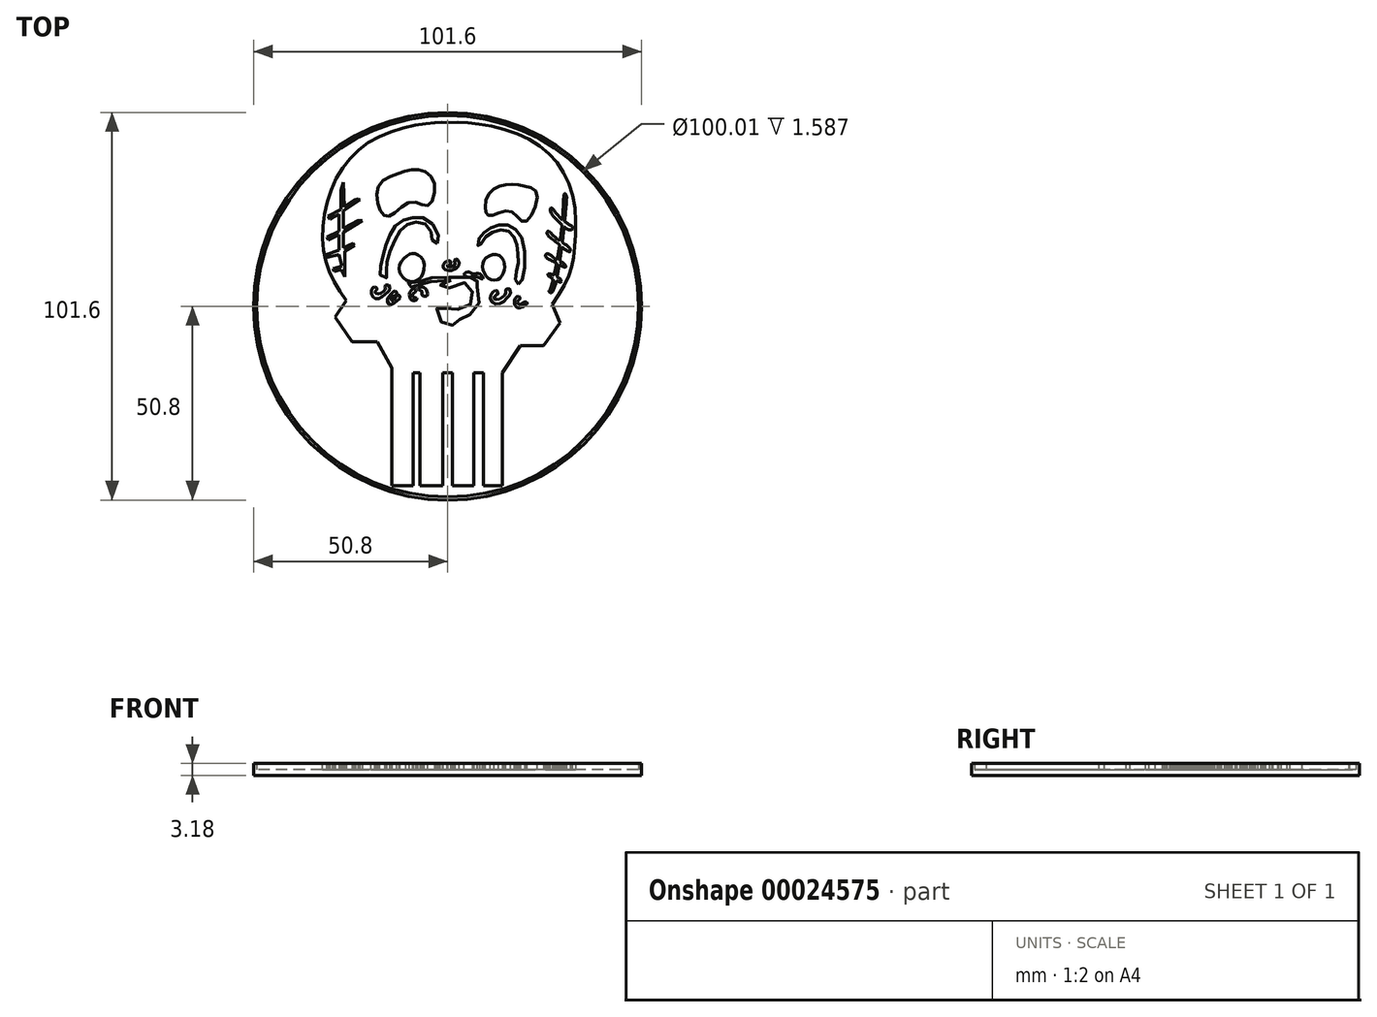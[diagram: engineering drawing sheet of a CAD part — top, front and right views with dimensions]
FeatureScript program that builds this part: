
annotation { "Feature Type Name" : "Feature", "Feature Type Description" : "" }
export const myFeature = defineFeature(function(context is Context, id is Id, definition is map)
    precondition{}
    {
        {
            var Q0;
            Q0=qCreatedBy(makeId("Top.planeOp"),FACE);
            var sketch = newSketch(context, id + "F0", { "sketchPlane" : qUnion([Q0])});
            skCircle(sketch, "E0", {"center": v(0, 0) * mm, "radius": 50.8 * mm});
            skSolve(sketch);
        }
        {
            var Q0;
            Q0 = qSketchRegion(id + "F0", true);
            extrude(context, id + "F1", {"entities" : qUnion([Q0]), "depth" : 1.59 * mm});
        }
        {
            var Q0;
            Q0=qCreatedBy(makeId("Top.planeOp"),FACE);
            var sketch = newSketch(context, id + "F2", { "sketchPlane" : qUnion([Q0])});
            skFitSpline(sketch, "E1", {"points": [v(-26.6, 1.46) * mm, v(-31.85, 11.54) * mm, v(-32.25, 24.2) * mm, v(-26.85, 37.18) * mm, v(-16.29, 45.16) * mm, v(-4.11, 48.07) * mm, v(0, 48.15) * mm], "startDerivative": vector(-36.73, 56.75) * mm, "endDerivative": vector(34.48, -1.2) * mm});
            skLineSegment(sketch, "E2", {"start": v(-26.6, 1.46) * mm, "end": v(-29.5, -2.79) * mm});
            skLineSegment(sketch, "E3", {"start": v(-29.5, -2.79) * mm, "end": v(-24.98, -9.3) * mm});
            skLineSegment(sketch, "E4", {"start": v(-24.98, -9.3) * mm, "end": v(-18.46, -9.3) * mm});
            skLineSegment(sketch, "E5", {"start": v(-18.46, -9.3) * mm, "end": v(-14.63, -16.12) * mm});
            skLineSegment(sketch, "E6", {"start": v(-14.63, -16.12) * mm, "end": v(-14.63, -47) * mm});
            skLineSegment(sketch, "E7", {"start": v(-14.63, -47) * mm, "end": v(-9.07, -47) * mm});
            skLineSegment(sketch, "E8", {"start": v(-9.07, -47) * mm, "end": v(-9.07, -17.46) * mm});
            skLineSegment(sketch, "E9", {"start": v(-9.07, -17.46) * mm, "end": v(-7.24, -17.46) * mm});
            skLineSegment(sketch, "E10", {"start": v(-7.24, -17.46) * mm, "end": v(-7.24, -47) * mm});
            skLineSegment(sketch, "E11", {"start": v(-7.24, -47) * mm, "end": v(-1.3, -47) * mm});
            skLineSegment(sketch, "E12", {"start": v(-1.3, -47) * mm, "end": v(-1.3, -17.46) * mm});
            skPoint(sketch, "E12.endSnap0", {"position": v(-8.15, -17.46) * mm});
            skLineSegment(sketch, "E13", {"start": v(-1.3, -17.46) * mm, "end": v(1.22, -17.46) * mm});
            skLineSegment(sketch, "E14", {"start": v(1.22, -17.46) * mm, "end": v(1.22, -47) * mm});
            skLineSegment(sketch, "E15", {"start": v(1.22, -47) * mm, "end": v(6.9, -47) * mm});
            skLineSegment(sketch, "E16", {"start": v(6.9, -47) * mm, "end": v(6.9, -17.46) * mm});
            skLineSegment(sketch, "E17", {"start": v(6.9, -17.46) * mm, "end": v(9.37, -17.46) * mm});
            skLineSegment(sketch, "E18", {"start": v(9.37, -17.46) * mm, "end": v(9.37, -47) * mm});
            skLineSegment(sketch, "E19", {"start": v(9.37, -47) * mm, "end": v(14.37, -47) * mm});
            skLineSegment(sketch, "E20", {"start": v(14.37, -47) * mm, "end": v(14.37, -17.46) * mm});
            skLineSegment(sketch, "E21", {"start": v(14.37, -17.46) * mm, "end": v(19.04, -10.32) * mm});
            skLineSegment(sketch, "E22", {"start": v(19.04, -10.32) * mm, "end": v(25.13, -10.32) * mm});
            skLineSegment(sketch, "E23", {"start": v(25.13, -10.32) * mm, "end": v(29.4, -4.4) * mm});
            skLineSegment(sketch, "E24", {"start": v(29.4, -4.4) * mm, "end": v(27.39, 0.48) * mm});
            skFitSpline(sketch, "E25", {"points": [v(27.39, 0.48) * mm, v(31.86, 8.27) * mm, v(33.2, 15.08) * mm, v(33.15, 27.34) * mm, v(28.8, 37.41) * mm, v(20.37, 44.27) * mm, v(8.12, 47.78) * mm, v(0, 48.15) * mm], "startDerivative": vector(38.96, 59.1) * mm, "endDerivative": vector(-60.1, -2.73) * mm});
            skFitSpline(sketch, "E26", {"points": [v(-18.15, 31.4) * mm, v(-12.69, 34.85) * mm, v(-7.7, 35.8) * mm, v(-3.58, 32.55) * mm, v(-5.11, 26.41) * mm, v(-9.43, 27.37) * mm, v(-14.99, 23.73) * mm, v(-17.39, 24.69) * mm, v(-18.15, 31.4) * mm]});
            skFitSpline(sketch, "E27", {"points": [v(10.8, 29.48) * mm, v(15.31, 31.88) * mm, v(20.2, 31.5) * mm, v(23.46, 29.2) * mm, v(20.1, 22.1) * mm, v(16.56, 24.88) * mm, v(11.38, 23.73) * mm, v(10.04, 24.59) * mm, v(10.8, 29.48) * mm]});
            skFitSpline(sketch, "E28", {"points": [v(-2.71, 16.53) * mm, v(-2.52, 18.93) * mm, v(-5.88, 23.06) * mm, v(-9.52, 23.15) * mm, v(-12.69, 22) * mm, v(-14.99, 18.93) * mm, v(-16.43, 15.2) * mm, v(-17.48, 10.97) * mm, v(-17.58, 8.1) * mm, v(-16.04, 7.42) * mm, v(-15.95, 9.25) * mm, v(-15.85, 12.12) * mm, v(-14.22, 16.44) * mm, v(-12.02, 20.37) * mm, v(-9.43, 21.8) * mm, v(-6.45, 21.9) * mm, v(-4.25, 19.32) * mm, v(-3.96, 17.1) * mm, v(-2.71, 16.53) * mm]});
            skFitSpline(sketch, "E29", {"points": [v(18.57, 5.8) * mm, v(19.72, 7.33) * mm, v(19.53, 17.5) * mm, v(16.37, 21.04) * mm, v(12.72, 21.14) * mm, v(9.75, 19.5) * mm, v(8.03, 17.3) * mm, v(8.12, 15.67) * mm, v(9.59, 17.62) * mm, v(12.16, 19.52) * mm, v(15.35, 19.86) * mm, v(17.59, 17.83) * mm, v(18.4, 14.5) * mm, v(18.4, 10.37) * mm, v(17.8, 7.05) * mm, v(18.57, 5.8) * mm]});
            skFitSpline(sketch, "E30", {"points": [v(-8.54, 13.8) * mm, v(-6.44, 12.03) * mm, v(-6.77, 8) * mm, v(-8.86, 6.55) * mm, v(-10.72, 6.8) * mm, v(-12.5, 8.8) * mm, v(-12.33, 11.39) * mm, v(-10.07, 13.57) * mm, v(-8.54, 13.8) * mm]});
            skFitSpline(sketch, "E31", {"points": [v(12.75, 13.57) * mm, v(14.76, 11.71) * mm, v(14.68, 9.05) * mm, v(13.31, 7.11) * mm, v(10.8, 7.2) * mm, v(9.28, 9.61) * mm, v(9.68, 12.27) * mm, v(12.75, 13.57) * mm]});
            skFitSpline(sketch, "E32", {"points": [v(2.17, 12.46) * mm, v(2.93, 11.74) * mm, v(2.65, 10.37) * mm, v(1.44, 9.56) * mm, v(0, 9.4) * mm, v(-1.26, 10.37) * mm, v(-0.41, 11.62) * mm, v(0.56, 11.94) * mm, v(0.8, 11.01) * mm, v(0, 10.85) * mm, v(0, 10.37) * mm, v(1.04, 10.37) * mm, v(2, 11.05) * mm, v(1.8, 11.7) * mm, v(2.17, 12.46) * mm]});
            skFitSpline(sketch, "E33", {"points": [v(9.24, 7.25) * mm, v(7.52, 7.68) * mm, v(5.21, 7.68) * mm, v(4.35, 8.35) * mm, v(5.02, 8.98) * mm, v(6.03, 8.83) * mm, v(6.41, 8.54) * mm, v(7.47, 8.54) * mm, v(8.67, 8.3) * mm, v(9.24, 7.25) * mm]});
            skFitSpline(sketch, "E34", {"points": [v(0.85, 6.77) * mm, v(-6, 6.1) * mm, v(-9.94, 5.04) * mm, v(-10.94, 5.81) * mm, v(-9.65, 6.17) * mm, v(-7.83, 6.25) * mm, v(-6.46, 7.08) * mm, v(-2.72, 7.45) * mm, v(2, 7.62) * mm, v(7.2, 7.33) * mm, v(7.54, 7.05) * mm, v(7.77, 6.55) * mm, v(6.91, 6.17) * mm, v(7.85, 4.97) * mm, v(8.28, 1.03) * mm, v(6.29, -1.99) * mm, v(4.23, -2.39) * mm, v(2.8, -3.81) * mm, v(1.95, -4.47) * mm, v(0.9, -5.12) * mm, v(-1.44, -4.33) * mm, v(-2.64, -1.9) * mm, v(-2.6, 0) * mm, v(-1.1, -0.53) * mm, v(0.78, -0.53) * mm, v(4.12, -0.73) * mm, v(6.17, 0.75) * mm, v(6.54, 3.23) * mm, v(5.92, 5.51) * mm, v(3, 6.02) * mm, v(-0.56, 4.57) * mm, v(-1.92, 5.17) * mm, v(-1.07, 6.14) * mm, v(0.85, 6.77) * mm]});
            skFitSpline(sketch, "E35", {"points": [v(12.47, 4.14) * mm, v(11.55, 3.36) * mm, v(11.18, 2.04) * mm, v(12.1, 0.72) * mm, v(14.16, 0.89) * mm, v(15.8, 2.38) * mm, v(16.5, 3.4) * mm, v(16.06, 4.65) * mm, v(15.25, 4.41) * mm, v(15.25, 4.31) * mm, v(15.15, 3.2) * mm, v(14.77, 2.68) * mm, v(13.72, 2) * mm, v(12.33, 1.87) * mm, v(12.33, 2.68) * mm, v(13.22, 3.16) * mm, v(12.98, 4.07) * mm, v(12.47, 4.14) * mm]});
            skFitSpline(sketch, "E36", {"points": [v(18.64, 2.65) * mm, v(17.9, 2.28) * mm, v(17.49, 1.23) * mm, v(17.63, 0.28) * mm, v(18.83, -0.49) * mm, v(20.25, 0.26) * mm, v(20.84, 0.69) * mm, v(20.65, 1.07) * mm, v(19.77, 0.93) * mm, v(19.14, 0.45) * mm, v(18.4, 0.74) * mm, v(18.52, 1.5) * mm, v(19, 2.05) * mm, v(18.64, 2.65) * mm]});
            skFitSpline(sketch, "E37", {"points": [v(-19.03, 5.1) * mm, v(-19.77, 4.65) * mm, v(-19.93, 3.1) * mm, v(-18.84, 1.94) * mm, v(-17.07, 2.62) * mm, v(-15.66, 3.71) * mm, v(-15.1, 4.65) * mm, v(-15.66, 5.57) * mm, v(-16.42, 5.29) * mm, v(-16.18, 4.65) * mm, v(-17.35, 3.51) * mm, v(-18.28, 3.27) * mm, v(-19.04, 3.63) * mm, v(-18.56, 4.32) * mm, v(-18.44, 4.65) * mm, v(-19.03, 5.1) * mm]});
            skFitSpline(sketch, "E38", {"points": [v(-13.72, 4.04) * mm, v(-15.13, 2.83) * mm, v(-15.86, 1.46) * mm, v(-15.01, 0.4) * mm, v(-13.2, 1.46) * mm, v(-12.51, 2.28) * mm, v(-12.91, 3.07) * mm, v(-13.92, 1.98) * mm, v(-14.65, 1.46) * mm, v(-14.8, 2.28) * mm, v(-14, 2.75) * mm, v(-13.32, 3.35) * mm, v(-13.72, 4.04) * mm]});
            skFitSpline(sketch, "E39", {"points": [v(-8.72, 4.65) * mm, v(-9.9, 3.6) * mm, v(-9.69, 1.86) * mm, v(-8.68, 1.46) * mm, v(-8, 1.94) * mm, v(-8.52, 2.28) * mm, v(-8.92, 2.28) * mm, v(-9.12, 3.23) * mm, v(-8.56, 3.63) * mm, v(-8.28, 4.36) * mm, v(-8.72, 4.65) * mm]});
            skFitSpline(sketch, "E40", {"points": [v(-6.76, 3.53) * mm, v(-6.59, 2.84) * mm, v(-5.53, 2.64) * mm, v(-5.25, 3.27) * mm, v(-5.62, 4.35) * mm, v(-6.41, 4.98) * mm, v(-7.36, 5) * mm, v(-7.78, 4.65) * mm, v(-7.24, 4.15) * mm, v(-6.67, 3.84) * mm, v(-6.76, 3.53) * mm]});
            skLineSegment(sketch, "E41", {"start": v(-27.33, 32.5) * mm, "end": v(-28, 30.29) * mm});
            skLineSegment(sketch, "E42", {"start": v(-28, 30.29) * mm, "end": v(-28, 25.35) * mm});
            skLineSegment(sketch, "E43", {"start": v(-28, 25.35) * mm, "end": v(-31.31, 23.53) * mm});
            skLineSegment(sketch, "E44", {"start": v(-31.31, 23.53) * mm, "end": v(-30.93, 22.83) * mm});
            skLineSegment(sketch, "E45", {"start": v(-30.93, 22.83) * mm, "end": v(-30.3, 23.18) * mm});
            skLineSegment(sketch, "E46", {"start": v(-30.3, 23.18) * mm, "end": v(-28.49, 24.15) * mm});
            skLineSegment(sketch, "E47", {"start": v(-28.49, 24.15) * mm, "end": v(-28.49, 19.65) * mm});
            skLineSegment(sketch, "E48", {"start": v(-28.49, 19.65) * mm, "end": v(-31.6, 18.16) * mm});
            skLineSegment(sketch, "E49", {"start": v(-31.6, 18.16) * mm, "end": v(-31.24, 17.4) * mm});
            skLineSegment(sketch, "E50", {"start": v(-31.24, 17.4) * mm, "end": v(-28.49, 18.71) * mm});
            skLineSegment(sketch, "E51", {"start": v(-28.49, 18.71) * mm, "end": v(-28.49, 14.66) * mm});
            skLineSegment(sketch, "E52", {"start": v(-28.49, 14.66) * mm, "end": v(-31.8, 13.6) * mm});
            skLineSegment(sketch, "E53", {"start": v(-31.8, 13.6) * mm, "end": v(-31.6, 12.84) * mm});
            skLineSegment(sketch, "E54", {"start": v(-31.6, 12.84) * mm, "end": v(-28.49, 13.62) * mm});
            skLineSegment(sketch, "E55", {"start": v(-28.49, 13.62) * mm, "end": v(-27.7, 10.47) * mm});
            skLineSegment(sketch, "E56", {"start": v(-27.7, 10.47) * mm, "end": v(-29.98, 9.9) * mm});
            skLineSegment(sketch, "E57", {"start": v(-29.98, 9.9) * mm, "end": v(-29.78, 9.1) * mm});
            skLineSegment(sketch, "E58", {"start": v(-29.78, 9.1) * mm, "end": v(-27.87, 9.59) * mm});
            skLineSegment(sketch, "E59", {"start": v(-27.87, 9.59) * mm, "end": v(-26.9, 7.76) * mm});
            skLineSegment(sketch, "E60", {"start": v(-26.9, 7.76) * mm, "end": v(-26.9, 14.47) * mm});
            skLineSegment(sketch, "E61", {"start": v(-26.9, 14.47) * mm, "end": v(-24.46, 15.95) * mm});
            skLineSegment(sketch, "E62", {"start": v(-24.46, 15.95) * mm, "end": v(-24.75, 16.43) * mm});
            skLineSegment(sketch, "E63", {"start": v(-24.75, 16.43) * mm, "end": v(-27.3, 15.36) * mm});
            skLineSegment(sketch, "E64", {"start": v(-27.3, 15.36) * mm, "end": v(-27.3, 19.45) * mm});
            skLineSegment(sketch, "E65", {"start": v(-27.3, 19.45) * mm, "end": v(-22.36, 22.5) * mm});
            skLineSegment(sketch, "E66", {"start": v(-22.36, 22.5) * mm, "end": v(-23.57, 22.5) * mm});
            skLineSegment(sketch, "E67", {"start": v(-23.57, 22.5) * mm, "end": v(-27.3, 20.38) * mm});
            skLineSegment(sketch, "E68", {"start": v(-27.3, 20.38) * mm, "end": v(-27.3, 24.93) * mm});
            skLineSegment(sketch, "E69", {"start": v(-27.3, 24.93) * mm, "end": v(-22.96, 27.87) * mm});
            skLineSegment(sketch, "E70", {"start": v(-22.96, 27.87) * mm, "end": v(-23.4, 28.12) * mm});
            skLineSegment(sketch, "E71", {"start": v(-23.4, 28.12) * mm, "end": v(-24.09, 27.9) * mm});
            skLineSegment(sketch, "E72", {"start": v(-24.09, 27.9) * mm, "end": v(-27.1, 25.98) * mm});
            skLineSegment(sketch, "E73", {"start": v(-27.1, 25.98) * mm, "end": v(-27.33, 32.5) * mm});
            skFitSpline(sketch, "E74", {"points": [v(30.45, 29.32) * mm, v(29.24, 15.3) * mm, v(26.66, 4.09) * mm, v(26.53, 3.94) * mm, v(27.21, 3.62) * mm, v(31.16, 28.17) * mm, v(31.12, 28.9) * mm, v(30.96, 29.3) * mm, v(30.72, 29.57) * mm], "startDerivative": vector(-2.79, -61.12) * mm, "endDerivative": vector(-7.53, 7.25) * mm});
            skLineSegment(sketch, "E75", {"start": v(30.45, 29.32) * mm, "end": v(30.72, 29.57) * mm});
            skFitSpline(sketch, "E76", {"points": [v(32.4, 21.05) * mm, v(29.53, 23.11) * mm, v(27.14, 25.75) * mm, v(26.9, 25.03) * mm, v(29.53, 21.77) * mm, v(31.98, 20) * mm, v(32.8, 20.33) * mm, v(32.4, 21.05) * mm]});
            skFitSpline(sketch, "E77.trimOffspring", {"points": [v(30.45, 29.32) * mm, v(29.24, 15.3) * mm, v(26.66, 4.09) * mm, v(26.53, 3.94) * mm, v(27.21, 3.62) * mm, v(31.16, 28.17) * mm, v(31.12, 28.9) * mm, v(30.96, 29.3) * mm, v(30.72, 29.57) * mm], "startDerivative": vector(-2.79, -61.12) * mm, "endDerivative": vector(-7.53, 7.25) * mm});
            skFitSpline(sketch, "E78.trimOffspring", {"points": [v(30.45, 29.32) * mm, v(29.24, 15.3) * mm, v(26.66, 4.09) * mm, v(26.53, 3.94) * mm, v(27.21, 3.62) * mm, v(31.16, 28.17) * mm, v(31.12, 28.9) * mm, v(30.96, 29.3) * mm, v(30.72, 29.57) * mm], "startDerivative": vector(-2.79, -61.12) * mm, "endDerivative": vector(-7.53, 7.25) * mm});
            skFitSpline(sketch, "E79", {"points": [v(26.28, 19.68) * mm, v(28.8, 17.57) * mm, v(31.99, 15.2) * mm, v(32.02, 14.31) * mm, v(31.68, 14.31) * mm, v(30.36, 15.2) * mm, v(27.95, 17.2) * mm, v(26.05, 19.06) * mm, v(26.28, 19.68) * mm]});
            skFitSpline(sketch, "E80", {"points": [v(30.9, 10.29) * mm, v(30.7, 10.96) * mm, v(28.26, 12.4) * mm, v(26.13, 13.76) * mm, v(25.59, 13.13) * mm, v(28.2, 11.5) * mm, v(30.9, 10.29) * mm]});
            skFitSpline(sketch, "E81", {"points": [v(29.76, 6.36) * mm, v(29.55, 7.1) * mm, v(29.21, 7.4) * mm, v(26.7, 8.52) * mm, v(26.26, 8.29) * mm, v(27.04, 7.54) * mm, v(28.37, 6.76) * mm, v(29.76, 6.36) * mm]});
            skFitSpline(sketch, "E82.trimOffspring", {"points": [v(30.45, 29.32) * mm, v(29.24, 15.3) * mm, v(26.66, 4.09) * mm, v(26.53, 3.94) * mm, v(27.21, 3.62) * mm, v(31.16, 28.17) * mm, v(31.12, 28.9) * mm, v(30.96, 29.3) * mm, v(30.72, 29.57) * mm], "startDerivative": vector(-2.79, -61.12) * mm, "endDerivative": vector(-7.53, 7.25) * mm});
            skSolve(sketch);
        }
        {
            var Q0;
            Q0 = qSketchRegion(id + "F2", true);
            extrude(context, id + "F3", {"entities" : qUnion([Q0]), "operationType" : NewBodyOperationType.ADD, "depth" : 3.17 * mm});
        }
        {
            var Q0;
            Q0=qCreatedBy(makeId("Top.planeOp"),FACE);
            var sketch = newSketch(context, id + "F4", { "sketchPlane" : qUnion([Q0]), "disableImprinting" : false});
            skCircle(sketch, "E83.0", {"center": v(0, 0) * mm, "radius": 50.8 * mm});
            skCircle(sketch, "E84", {"center": v(0, 0) * mm, "radius": 50 * mm});
            skSolve(sketch);
        }
        {
            var Q0;
            Q0 = qSketchRegion(id + "F4", true);
            extrude(context, id + "F5", {"entities" : qUnion([Q0]), "operationType" : NewBodyOperationType.ADD, "depth" : 3.17 * mm});
        }
    });
